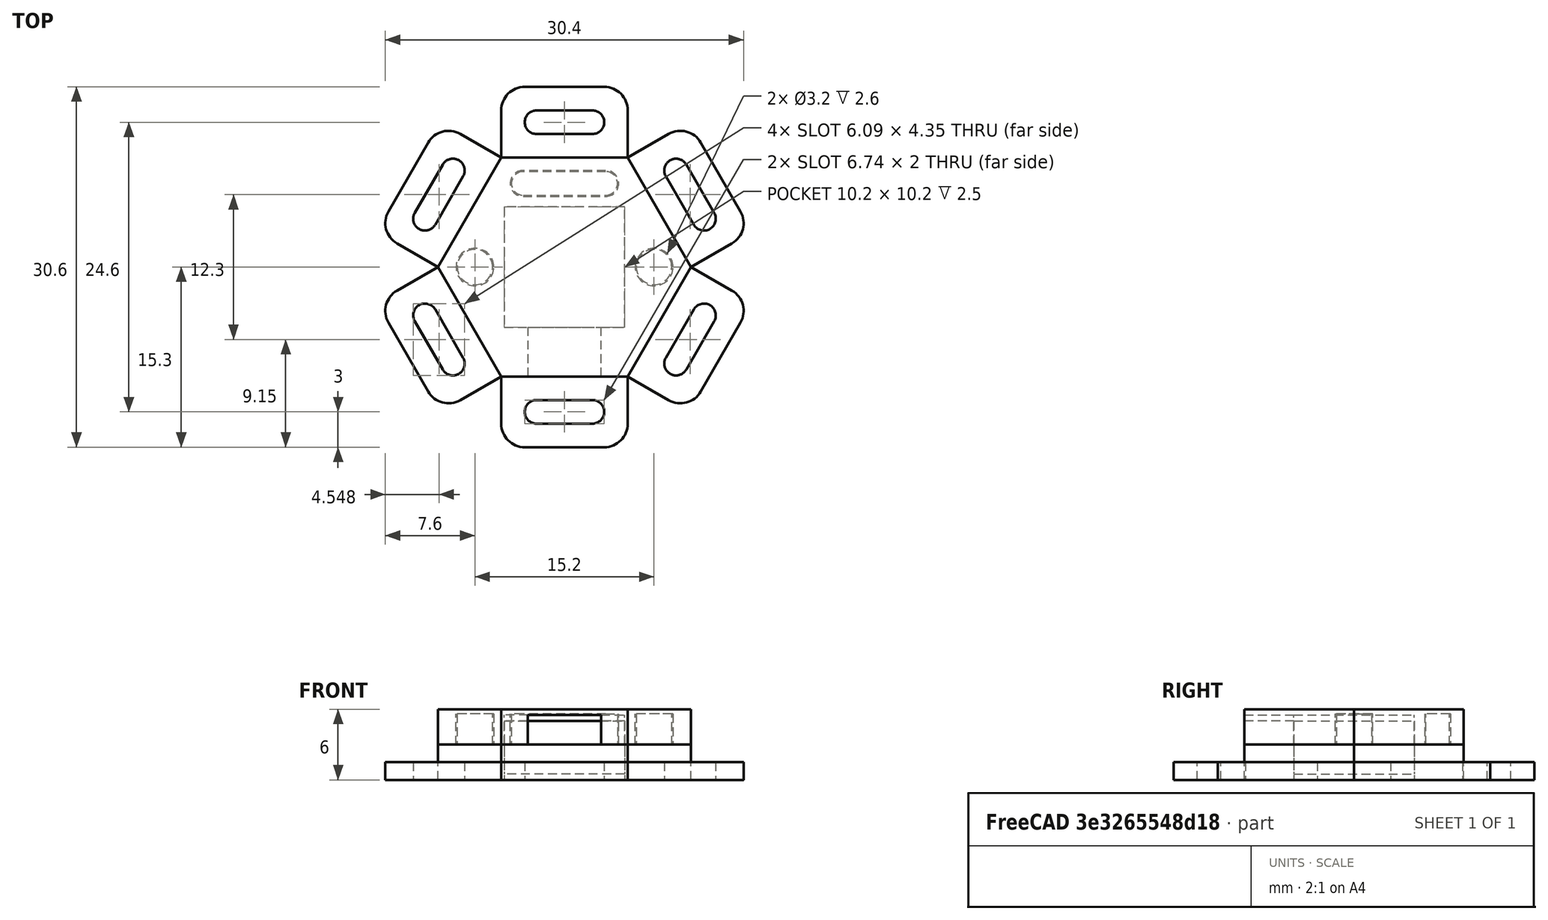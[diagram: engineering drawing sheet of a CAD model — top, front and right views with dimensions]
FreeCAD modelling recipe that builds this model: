
FCSTD DOCUMENT  (FreeCAD 1.0R39109 (Git))
Label: vybronics_hexagon
License: Creative Commons Attribution 4.0
LicenseURL: https://creativecommons.org/licenses/by/4.0/
objects: TechDraw::DrawViewDimension×15, TechDraw::DrawProjGroupItem×8, Sketcher::SketchObject×7, PartDesign::SubShapeBinder×7, PartDesign::Body×6, PartDesign::Pad×5, PartDesign::Pocket×3, PartDesign::FeatureBase×2, PartDesign::Plane×2, TechDraw::DrawProjGroup×2, PartDesign::Boolean×1, Part::FeaturePython×1, Part::Compound×1, TechDraw::DrawSVGTemplate×1, TechDraw::DrawViewImage×1, TechDraw::DrawPage×1
note: 82 computed .brp shape members not serialized (recipe doc carries the construction recipe); baked Part::Feature solids carry a one-line shape summary decoded from their .brp

FEATURE [Sketcher::SketchObject] Sketch
  ArcFitTolerance = 0
  AttachmentSupport = -> [XY_Plane]
  FullyConstrained = true
  MakeInternals = false
  MapMode = 5
  sketch-geometry (5):
    g0: LineSegment StartX=5.1 StartY=-5.1 StartZ=0 EndX=5.1 EndY=5.1 EndZ=0
    g1: LineSegment StartX=5.1 StartY=5.1 StartZ=0 EndX=-5.1 EndY=5.1 EndZ=0
    g2: LineSegment StartX=-5.1 StartY=5.1 StartZ=0 EndX=-5.1 EndY=-5.1 EndZ=0
    g3: LineSegment StartX=-5.1 StartY=-5.1 StartZ=0 EndX=5.1 EndY=-5.1 EndZ=0
    g4: GeomPoint [constr] X=0 Y=-1e-16 Z=0
  constraints (12):
    c: Coincident(g0,g1)
    c: Coincident(g1,g2)
    c: Coincident(g2,g3)
    c: Coincident(g3,g0)
    c: Horizontal(g1)
    c: Horizontal(g3)
    c: Vertical(g0)
    c: Vertical(g2)
    c: Symmetric(g1,g0,g4)
    c: Coincident(g4,g-1)
    c: DistanceX(g1,g1) = 10.2
    c: DistanceY(g0,g0) = 10.2
FEATURE [PartDesign::Pad] Pad
  Direction = (0,0,1)
  Length = 5
  Length2 = 10
  Profile = -> Sketch
  ReferenceAxis = -> Sketch [N_Axis]
  Suppressed = false
  Type = 0
FEATURE [PartDesign::Body] Body
  AllowCompound = false
  Group = -> [Sketch,Pad]
  Origin = -> Origin
  Tip = -> Pad
FEATURE [PartDesign::SubShapeBinder] Binder  label="actuator_area"
  BindCopyOnChange = 0
  BindMode = 0
  ClaimChildren = false
  Context = -> Body001 [Binder.]
  Fuse = false
  MakeFace = true
  OffsetFill = false
  OffsetIntersection = false
  OffsetJoinType = 0
  OffsetOpenResult = false
  PartialLoad = false
  Relative = true
  Support = -> [Body[Pad.Face5]]
  _Version = 2
FEATURE [Sketcher::SketchObject] Sketch001
  ArcFitTolerance = 0
  AttachmentSupport = -> [XY_Plane001]
  ExternalGeometry = -> [Binder]
  FullyConstrained = true
  MakeInternals = false
  MapMode = 5
  sketch-geometry (5):
    g0: LineSegment StartX=-3.1 StartY=-5.1 StartZ=0 EndX=-3.1 EndY=-9.3 EndZ=0
    g1: LineSegment StartX=-3.1 StartY=-9.3 StartZ=0 EndX=3.1 EndY=-9.3 EndZ=0
    g2: LineSegment StartX=3.1 StartY=-9.3 StartZ=0 EndX=3.1 EndY=-5.1 EndZ=0
    g3: LineSegment StartX=3.1 StartY=-5.1 StartZ=0 EndX=-3.1 EndY=-5.1 EndZ=0
    g4: GeomPoint [constr] X=0 Y=-7.2 Z=0
  constraints (13):
    c: Coincident(g0,g1)
    c: Coincident(g1,g2)
    c: Coincident(g2,g3)
    c: Coincident(g3,g0)
    c: Horizontal(g1)
    c: Horizontal(g3)
    c: Vertical(g0)
    c: Vertical(g2)
    c: Symmetric(g1,g0,g4)
    c: PointOnObject(g4,g-2)
    c: PointOnObject(g0,g-4)
    c: DistanceX(g1,g1) = 6.2
    c: DistanceY(g2,g2) = 4.2
FEATURE [PartDesign::Pad] Pad001
  Direction = (0,0,1)
  Length = 2
  Length2 = 10
  Profile = -> Sketch001
  ReferenceAxis = -> Sketch001 [N_Axis]
  Suppressed = false
  Type = 0
FEATURE [PartDesign::Boolean] Boolean
  BaseFeature = -> Pad001
  Group = -> [Body]
  Suppressed = false
  Type = 0
  UsePlacement = false
FEATURE [PartDesign::Body] Body001  label="actuator"
  AllowCompound = false
  Group = -> [Sketch001,Binder,Pad001,Boolean]
  Origin = -> Origin001
  Placement = pos=(-6e-16,0,5) rot=(0,1,0;3.14159rad)
  Tip = -> Boolean
FEATURE [PartDesign::SubShapeBinder] Binder001
  BindCopyOnChange = 0
  BindMode = 0
  ClaimChildren = false
  Context = -> Body002 [Binder001.]
  Fuse = false
  MakeFace = true
  OffsetFill = false
  OffsetIntersection = false
  OffsetJoinType = 0
  OffsetOpenResult = false
  PartialLoad = false
  Relative = true
  Support = -> [Body001[Boolean.Face4],Binder002]
  _Version = 2
FEATURE [Sketcher::SketchObject] Sketch002
  ArcFitTolerance = 0
  AttachmentSupport = -> [XY_Plane002]
  ExternalGeometry = -> [Binder001]
  FullyConstrained = true
  MakeInternals = false
  MapMode = 5
  sketch-geometry (14):
    g0: LineSegment [constr] StartX=-5.1 StartY=5.1 StartZ=0 EndX=5.1 EndY=5.1 EndZ=0
    g1: LineSegment [constr] StartX=5.1 StartY=5.1 StartZ=0 EndX=5.1 EndY=-9.3 EndZ=0
    g2: LineSegment [constr] StartX=5.1 StartY=-9.3 StartZ=0 EndX=-5.1 EndY=-9.3 EndZ=0
    g3: LineSegment [constr] StartX=-5.1 StartY=-9.3 StartZ=0 EndX=-5.1 EndY=5.1 EndZ=0
    g4: LineSegment [constr] StartX=5.1 StartY=5.1 StartZ=0 EndX=-5.1 EndY=-9.3 EndZ=0
    g5: LineSegment [constr] StartX=-5.1 StartY=5.1 StartZ=0 EndX=5.1 EndY=-9.3 EndZ=0
    g6: GeomPoint [constr] X=0 Y=-2.1 Z=0
    g7: LineSegment StartX=-5.36936 StartY=9.3 StartZ=0 EndX=-10.7387 EndY=1.2e-15 EndZ=0
    g8: LineSegment StartX=-10.7387 StartY=1.2e-15 StartZ=0 EndX=-5.36936 EndY=-9.3 EndZ=0
    g9: LineSegment StartX=-5.36936 StartY=-9.3 StartZ=0 EndX=5.36936 EndY=-9.3 EndZ=0
    g10: LineSegment StartX=5.36936 StartY=-9.3 StartZ=0 EndX=10.7387 EndY=1.9e-15 EndZ=0
    g11: LineSegment StartX=10.7387 StartY=1.9e-15 StartZ=0 EndX=5.36936 EndY=9.3 EndZ=0
    g12: LineSegment StartX=5.36936 StartY=9.3 StartZ=0 EndX=-5.36936 EndY=9.3 EndZ=0
    g13: Circle [constr] CenterX=0 CenterY=0 CenterZ=0 NormalX=0 NormalY=0 NormalZ=1 AngleXU=0 Radius=10.7387
  constraints (31):
    c: Coincident(g0,g1)
    c: Coincident(g1,g2)
    c: Coincident(g2,g3)
    c: Coincident(g3,g0)
    c: Horizontal(g2)
    c: Vertical(g1)
    c: Vertical(g3)
    c: Coincident(g0,g-5)
    c: Coincident(g0,g-4)
    c: PointOnObject(g1,g-9)
    c: Coincident(g4,g0)
    c: Coincident(g4,g2)
    c: Coincident(g5,g0)
    c: Coincident(g5,g1)
    c: PointOnObject(g6,g5)
    c: PointOnObject(g6,g-2)
    c: Coincident(g7,g8)
    c: Coincident(g8,g9)
    c: Coincident(g9,g10)
    c: Coincident(g10,g11)
    c: Coincident(g11,g12)
    c: Coincident(g12,g7)
    c: Equal(g7, g8-g12) x5
    c: PointOnObject(g7,g13)
    c: PointOnObject(g8,g13)
    c: PointOnObject(g9,g13)
    c: PointOnObject(g10,g13)
    c: PointOnObject(g11,g13)
    c: PointOnObject(g12,g13)
    c: Coincident(g13,g-1)
    c: Tangent(g9,g2)
FEATURE [PartDesign::SubShapeBinder] Binder002
  BindCopyOnChange = 0
  BindMode = 0
  ClaimChildren = false
  Context = -> Body002 [Binder002.]
  Fuse = false
  MakeFace = true
  OffsetFill = false
  OffsetIntersection = false
  OffsetJoinType = 0
  OffsetOpenResult = false
  PartialLoad = false
  Relative = true
  Support = -> [Body001[Boolean.Face10]]
  _Version = 2
FEATURE [PartDesign::Pad] Pad002
  Direction = (0,0,1)
  Length = 3
  Length2 = 10
  Profile = -> Sketch002
  ReferenceAxis = -> Sketch002 [N_Axis]
  Suppressed = false
  Type = 0
FEATURE [PartDesign::Body] Body002
  AllowCompound = false
  Group = -> [Binder001,Sketch002,Binder002,Pad002]
  Origin = -> Origin002
  Placement = pos=(0,0,3) rot=(0,0,1;0rad)
  Tip = -> Pad002
FEATURE [PartDesign::FeatureBase] Clone
  BaseFeature = -> Body002
  Suppressed = false
FEATURE [PartDesign::SubShapeBinder] Binder003
  BindCopyOnChange = 0
  BindMode = 0
  ClaimChildren = false
  Context = -> Body004 [Binder003.]
  Fuse = false
  MakeFace = true
  OffsetFill = false
  OffsetIntersection = false
  OffsetJoinType = 0
  OffsetOpenResult = false
  PartialLoad = false
  Relative = true
  Support = -> [Body003[Clone.Face7]]
  _Version = 2
FEATURE [Sketcher::SketchObject] Sketch003
  ArcFitTolerance = 0
  AttachmentSupport = -> [XY_Plane004]
  ExternalGeometry = -> [Binder003]
  FullyConstrained = true
  MakeInternals = false
  MapMode = 5
  sketch-geometry (10):
    g0: LineSegment StartX=-5.36936 StartY=9.3 StartZ=0 EndX=5.36936 EndY=9.3 EndZ=0
    g1: LineSegment StartX=5.36936 StartY=9.3 StartZ=0 EndX=5.36936 EndY=13.3 EndZ=0
    g2: LineSegment StartX=3.36936 StartY=15.3 StartZ=0 EndX=-3.36936 EndY=15.3 EndZ=0
    g3: LineSegment StartX=-5.36936 StartY=13.3 StartZ=0 EndX=-5.36936 EndY=9.3 EndZ=0
    g4: ArcOfCircle CenterX=-3.36936 CenterY=13.3 CenterZ=0 NormalX=0 NormalY=0 NormalZ=1 AngleXU=0 Radius=2 StartAngle=1.5708 EndAngle=3.14159
    g5: ArcOfCircle CenterX=3.36936 CenterY=13.3 CenterZ=0 NormalX=0 NormalY=0 NormalZ=1 AngleXU=0 Radius=2 StartAngle=2e-16 EndAngle=1.5708
    g6: ArcOfCircle CenterX=-2.36936 CenterY=12.3 CenterZ=0 NormalX=0 NormalY=0 NormalZ=1 AngleXU=0 Radius=1 StartAngle=1.5708 EndAngle=4.71239
    g7: ArcOfCircle CenterX=2.36936 CenterY=12.3 CenterZ=0 NormalX=0 NormalY=0 NormalZ=1 AngleXU=0 Radius=1 StartAngle=4.71239 EndAngle=7.85398
    g8: LineSegment StartX=-2.36936 StartY=11.3 StartZ=0 EndX=2.36936 EndY=11.3 EndZ=0
    g9: LineSegment StartX=2.36936 StartY=13.3 StartZ=0 EndX=-2.36936 EndY=13.3 EndZ=0
  constraints (23):
    c: Coincident(g0,g1)
    c: Coincident(g3,g0)
    c: Horizontal(g2)
    c: Vertical(g1)
    c: Vertical(g3)
    c: Coincident(g0,g-3)
    c: Coincident(g0,g-3)
    c: Tangent(g2,g4) = -1.5708
    c: Tangent(g3,g4) = -1.5708
    c: Tangent(g1,g5) = -1.5708
    c: Tangent(g2,g5) = -1.5708
    c: Radius(g4) = 2
    c: Equal(g5,g4)
    c: DistanceY(g1,g1) = 4
    c: Tangent(g6,g8) = -1.5708
    c: Tangent(g8,g7) = -1.5708
    c: Tangent(g7,g9) = -1.5708
    c: Tangent(g9,g6) = -1.5708
    c: Equal(g6,g7)
    c: Symmetric(g6,g7,g-2)
    c: DistanceY(g6,g2) = 2
    c: Radius(g7) = 1
    c: DistanceX(g7,g0) = 3
FEATURE [PartDesign::Pad] Pad003
  Direction = (0,0,1)
  Length = 1.5
  Length2 = 10
  Profile = -> Sketch003
  ReferenceAxis = -> Sketch003 [N_Axis]
  Suppressed = false
  Type = 0
FEATURE [PartDesign::Body] Body004
  AllowCompound = false
  Group = -> [Binder003,Sketch003,Pad003]
  Origin = -> Origin004
  Tip = -> Pad003
FEATURE [Part::FeaturePython] Array  label="bottom_holder"  # Draft array (typed FeaturePython)
  AlwaysSyncPlacement = false
  Angle = 360
  ArrayType = 1
  Axis = (0,0,1)
  Base = -> Body004
  Center = (0,0,0)
  Count = 6
  ExpandArray = false
  Fuse = true
  IntervalAxis = (0,0,0)
  IntervalX = (50,0,0)
  IntervalY = (0,50,0)
  IntervalZ = (0,0,50)
  NumberCircles = 3
  NumberPolar = 6
  NumberX = 2
  NumberY = 2
  NumberZ = 1
  PlacementList = 6 placements: [(0,0,0),(0,0,0),(0,0,0),(0,0,0),(0,0,0),(0,0,0)]
  RadialDistance = 50
  ScaleList = (6) [(1,1,1),(1,1,1),(1,1,1),(1,1,1),(1,1,1),(1,1,1)]
  Symmetry = 1
  TangentialDistance = 25
FEATURE [PartDesign::Plane] DatumPlane
  AttachmentSupport = -> [Clone]
  Length = 60
  MapMode = 5
  Placement = pos=(0,0,3) rot=(0,0,1;0rad)
  ResizeMode = 0
  Width = 60
FEATURE [PartDesign::SubShapeBinder] Binder004
  BindCopyOnChange = 0
  BindMode = 0
  ClaimChildren = false
  Context = -> Body003 [Binder004.]
  Fuse = false
  MakeFace = true
  OffsetFill = false
  OffsetIntersection = false
  OffsetJoinType = 0
  OffsetOpenResult = false
  PartialLoad = false
  Relative = true
  Support = -> [Body001[Boolean.Face4]]
  _Version = 2
FEATURE [Sketcher::SketchObject] Sketch004
  ArcFitTolerance = 0
  AttachmentSupport = -> [DatumPlane]
  ExternalGeometry = -> [Binder004]
  FullyConstrained = true
  MakeInternals = false
  MapMode = 5
  Placement = pos=(0,0,3) rot=(0,0,1;0rad)
  sketch-geometry (6):
    g0: Circle CenterX=-7.6 CenterY=0 CenterZ=0 NormalX=0 NormalY=0 NormalZ=1 AngleXU=0 Radius=1.5
    g1: Circle CenterX=7.6 CenterY=0 CenterZ=0 NormalX=0 NormalY=0 NormalZ=1 AngleXU=0 Radius=1.5
    g2: ArcOfCircle CenterX=-3.5 CenterY=7.1 CenterZ=0 NormalX=0 NormalY=0 NormalZ=1 AngleXU=0 Radius=1 StartAngle=1.5708 EndAngle=4.71239
    g3: ArcOfCircle CenterX=3.5 CenterY=7.1 CenterZ=0 NormalX=0 NormalY=0 NormalZ=1 AngleXU=0 Radius=1 StartAngle=4.71239 EndAngle=7.85398
    g4: LineSegment StartX=-3.5 StartY=6.1 StartZ=0 EndX=3.5 EndY=6.1 EndZ=0
    g5: LineSegment StartX=3.5 StartY=8.1 StartZ=0 EndX=-3.5 EndY=8.1 EndZ=0
  constraints (15):
    c: PointOnObject(g0,g-1)
    c: Diameter(g0) = 3
    c: Equal(g0,g1) = 3
    c: Distance(g0,g-4) = 1
    c: PointOnObject(g1,g-1)
    c: Distance(g1,g-5) = 1
    c: Tangent(g2,g4) = -1.5708
    c: Tangent(g4,g3) = -1.5708
    c: Tangent(g3,g5) = -1.5708
    c: Tangent(g5,g2) = -1.5708
    c: Equal(g2,g3)
    c: Symmetric(g2,g3,g-2)
    c: Radius(g2) = 1
    c: Distance(g2,g-3) = 1
    c: DistanceX(g5,g5) = 7
FEATURE [PartDesign::Pad] Pad004
  BaseFeature = -> Clone
  Direction = (0,0,1)
  Length = 2.6
  Length2 = 10
  Profile = -> Sketch004
  ReferenceAxis = -> Sketch004 [N_Axis]
  Suppressed = false
  Type = 0
FEATURE [PartDesign::FeatureBase] Clone001
  BaseFeature = -> Body002
  Placement = pos=(0,0,3) rot=(0,0,1;0rad)
  Suppressed = false
FEATURE [PartDesign::SubShapeBinder] Binder005
  BindCopyOnChange = 0
  BindMode = 0
  ClaimChildren = false
  Context = -> Body005 [Binder005.]
  Fuse = false
  MakeFace = true
  Offset = 0.1
  OffsetFill = false
  OffsetIntersection = false
  OffsetJoinType = 0
  OffsetOpenResult = false
  PartialLoad = false
  Relative = true
  Support = -> [Body003[Pad004.Face15,Pad004.Face16,Pad004.Face17]]
  _Version = 2
FEATURE [PartDesign::Pocket] Pocket
  BaseFeature = -> Clone001
  Direction = (0,0,-1)
  Length = 5
  Length2 = 5
  Placement = pos=(0,0,3) rot=(0,0,1;0rad)
  Profile = -> Binder005
  Suppressed = false
  Type = 0
FEATURE [Sketcher::SketchObject] Sketch005
  ArcFitTolerance = 0
  AttachmentSupport = -> [DatumPlane]
  ExternalGeometry = -> [Binder004]
  FullyConstrained = true
  MakeInternals = false
  MapMode = 5
  Placement = pos=(0,0,3) rot=(0,0,1;0rad)
  sketch-geometry (5):
    g0: LineSegment StartX=5.1 StartY=-5.1 StartZ=0 EndX=5.1 EndY=5.1 EndZ=0
    g1: LineSegment StartX=5.1 StartY=5.1 StartZ=0 EndX=-5.1 EndY=5.1 EndZ=0
    g2: LineSegment StartX=-5.1 StartY=5.1 StartZ=0 EndX=-5.1 EndY=-5.1 EndZ=0
    g3: LineSegment StartX=-5.1 StartY=-5.1 StartZ=0 EndX=5.1 EndY=-5.1 EndZ=0
    g4: GeomPoint [constr] X=0 Y=0 Z=0
  constraints (11):
    c: Coincident(g0,g1)
    c: Coincident(g1,g2)
    c: Coincident(g2,g3)
    c: Coincident(g3,g0)
    c: Horizontal(g1)
    c: Horizontal(g3)
    c: Vertical(g0)
    c: Vertical(g2)
    c: Symmetric(g1,g0,g4)
    c: Coincident(g4,g-1)
    c: Coincident(g1,g-3)
FEATURE [PartDesign::Pocket] Pocket001
  BaseFeature = -> Pad004
  Direction = (0,0,-1)
  Length = 2.5
  Length2 = 5
  Profile = -> Sketch005
  ReferenceAxis = -> Sketch005 [N_Axis]
  Suppressed = false
  Type = 0
FEATURE [PartDesign::Body] Body003  label="bottom_platform"
  AllowCompound = false
  Group = -> [Clone,DatumPlane,Sketch004,Binder004,Pad004,Sketch005,Pocket001]
  Origin = -> Origin003
  Tip = -> Pocket001
FEATURE [Part::Compound] Compound  label="bottom"
  Links = -> [Body003,Array]
FEATURE [PartDesign::SubShapeBinder] Binder006
  BindCopyOnChange = 0
  BindMode = 0
  ClaimChildren = false
  Context = -> Body005 [Binder006.]
  Fuse = false
  MakeFace = true
  OffsetFill = false
  OffsetIntersection = false
  OffsetJoinType = 0
  OffsetOpenResult = false
  PartialLoad = false
  Relative = true
  Support = -> [Body001[Boolean.Face10,Boolean.Face4]]
  _Version = 2
FEATURE [PartDesign::Plane] DatumPlane001
  AttachmentSupport = -> [Pocket]
  Length = 60
  MapMode = 5
  Placement = pos=(0,0,3) rot=(1,0,0;3.14159rad)
  ResizeMode = 0
  Width = 60
FEATURE [Sketcher::SketchObject] Sketch006
  ArcFitTolerance = 0
  AttachmentSupport = -> [DatumPlane001]
  ExternalGeometry = -> [Binder006]
  FullyConstrained = true
  MakeInternals = false
  MapMode = 5
  Placement = pos=(0,0,3) rot=(1,0,0;3.14159rad)
  sketch-geometry (8):
    g0: LineSegment StartX=-3.1 StartY=9.3 StartZ=0 EndX=3.1 EndY=9.3 EndZ=0
    g1: LineSegment StartX=3.1 StartY=9.3 StartZ=0 EndX=3.1 EndY=5.1 EndZ=0
    g2: LineSegment StartX=3.1 StartY=5.1 StartZ=0 EndX=5.1 EndY=5.1 EndZ=0
    g3: LineSegment StartX=5.1 StartY=5.1 StartZ=0 EndX=5.1 EndY=-5.1 EndZ=0
    g4: LineSegment StartX=5.1 StartY=-5.1 StartZ=0 EndX=-5.1 EndY=-5.1 EndZ=0
    g5: LineSegment StartX=-5.1 StartY=-5.1 StartZ=0 EndX=-5.1 EndY=5.1 EndZ=0
    g6: LineSegment StartX=-5.1 StartY=5.1 StartZ=0 EndX=-3.1 EndY=5.1 EndZ=0
    g7: LineSegment StartX=-3.1 StartY=5.1 StartZ=0 EndX=-3.1 EndY=9.3 EndZ=0
  constraints (16):
    c: Coincident(g-6,g0)
    c: Coincident(g0,g-10)
    c: Coincident(g0,g1)
    c: Coincident(g1,g-10)
    c: Coincident(g1,g2)
    c: Coincident(g2,g-9)
    c: Coincident(g2,g3)
    c: Coincident(g3,g-8)
    c: Coincident(g3,g4)
    c: Coincident(g4,g-7)
    c: Coincident(g4,g5)
    c: Coincident(g5,g-4)
    c: Coincident(g5,g6)
    c: Coincident(g6,g-6)
    c: Coincident(g6,g7)
    c: Coincident(g7,g0)
FEATURE [PartDesign::Pocket] Pocket002
  BaseFeature = -> Pocket
  Direction = (0,0,1)
  Length = 2.5
  Length2 = 5
  Placement = pos=(0,0,3) rot=(0,0,1;0rad)
  Profile = -> Sketch006
  ReferenceAxis = -> Sketch006 [N_Axis]
  Suppressed = false
  Type = 0
FEATURE [PartDesign::Body] Body005  label="top"
  AllowCompound = false
  Group = -> [Clone001,Binder005,Pocket,Binder006,DatumPlane001,Sketch006,Pocket002]
  Origin = -> Origin005
  Tip = -> Pocket002
FEATURE [TechDraw::DrawSVGTemplate] Template
  EditableTexts = Designed_by_Name=Dennis Wittchen; Drawing_number=1; FC-Date=Jan 17 2024; FC-SC=Scale; FC-SH=1; FC-Title=Vybronics case; Subtitle=modular system; Weight=Weight
  Height = 210
  Orientation = 1
  Template = /Applications/FreeCAD.app/Contents/Resources/share/Mod/TechDraw/Templates/A4_LandscapeTD.svg
  Width = 297
FEATURE [TechDraw::DrawViewImage] ActiveView
  Height = 100
  ImageFile = <userpath>/Library/Caches/FreeCAD/Cache/FreeCAD_Doc_c7f0712c-06d2-497b-9420-8f54370957ff_efbe33_32540/PageActiveView41v21o.png
  LockPosition = false
  Rotation = 0
  Scale = 2
  ScaleType = 2
  Width = 100
  X = 245.698
  Y = 86.6817
FEATURE [TechDraw::DrawProjGroupItem] ProjItem  label="Front"
  CoarseView = false
  Direction = (0,0,1)
  Focus = 100
  HardHidden = false
  IsoCount = 0
  IsoHidden = false
  IsoVisible = false
  LockPosition = true
  Perspective = false
  Rotation = 0
  RotationVector = (1,0,0)
  Scale = 2
  ScaleType = 2
  ScrubCount = 0
  SeamHidden = false
  SeamVisible = false
  SmoothHidden = false
  SmoothVisible = true
  Source = -> [Body005]
  Type = 0
  X = 0
  XDirection = (1,0,0)
  Y = 0
FEATURE [TechDraw::DrawProjGroupItem] ProjItem001  label="Bottom"
  CoarseView = false
  Direction = (0,-1,0)
  Focus = 100
  HardHidden = false
  IsoCount = 0
  IsoHidden = false
  IsoVisible = false
  LockPosition = false
  Perspective = false
  Rotation = 0
  RotationVector = (1,0,0)
  Scale = 2
  ScaleType = 2
  ScrubCount = 0
  SeamHidden = false
  SeamVisible = false
  SmoothHidden = false
  SmoothVisible = true
  Source = -> [Body005]
  Type = 5
  X = 0
  XDirection = (1,0,0)
  Y = 33.9717
FEATURE [TechDraw::DrawProjGroupItem] ProjItem002  label="Rear"
  CoarseView = false
  Direction = (0,0,-1)
  Focus = 100
  HardHidden = false
  IsoCount = 0
  IsoHidden = false
  IsoVisible = false
  LockPosition = false
  Perspective = false
  Rotation = 0
  RotationVector = (1,0,0)
  Scale = 2
  ScaleType = 2
  ScrubCount = 0
  SeamHidden = false
  SeamVisible = false
  SmoothHidden = false
  SmoothVisible = true
  Source = -> [Body005]
  Type = 3
  X = 46.4774
  XDirection = (-1,0,0)
  Y = 0
FEATURE [TechDraw::DrawProjGroup] ProjGroup
  Anchor = -> ProjItem
  AutoDistribute = false
  LockPosition = false
  ProjectionType = 0
  Rotation = 0
  Scale = 2
  ScaleType = 2
  Source = -> [Body005]
  Views = -> [ProjItem,ProjItem001,ProjItem002]
  X = 42.3498
  Y = 45.659
  spacingX = 25
  spacingY = 25
FEATURE [TechDraw::DrawViewDimension] Dimension
  AngleOverride = false
  Arbitrary = false
  ArbitraryTolerances = false
  EqualTolerance = true
  ExtensionAngle = 0
  FormatSpec = %.2w
  FormatSpecOverTolerance = %+.2w
  FormatSpecUnderTolerance = %+.2w
  Inverted = false
  LineAngle = 0
  LockPosition = false
  MeasureType = 1
  OverTolerance = 0
  References2D = -> [ProjItem]
  Rotation = 0
  ScaleType = 0
  TheoreticalExact = false
  Type = 0
  UnderTolerance = 0
  X = -22.3709
  Y = 14.2955
FEATURE [TechDraw::DrawViewDimension] Dimension001
  AngleOverride = false
  Arbitrary = false
  ArbitraryTolerances = false
  EqualTolerance = true
  ExtensionAngle = 0
  FormatSpec = %.2w
  FormatSpecOverTolerance = %+.2w
  FormatSpecUnderTolerance = %+.2w
  Inverted = false
  LineAngle = 0
  LockPosition = false
  MeasureType = 1
  OverTolerance = 0
  References2D = -> [ProjItem]
  Rotation = 0
  ScaleType = 0
  TheoreticalExact = false
  Type = 1
  UnderTolerance = 0
  X = -1.45647
  Y = -26.1729
FEATURE [TechDraw::DrawViewDimension] Dimension003
  AngleOverride = false
  Arbitrary = false
  ArbitraryTolerances = false
  EqualTolerance = true
  ExtensionAngle = 0
  FormatSpec = %.2w
  FormatSpecOverTolerance = %+.2w
  FormatSpecUnderTolerance = %+.2w
  Inverted = false
  LineAngle = 0
  LockPosition = false
  MeasureType = 1
  OverTolerance = 0
  References2D = -> [ProjItem002]
  Rotation = 0
  ScaleType = 0
  TheoreticalExact = false
  Type = 2
  UnderTolerance = 0
  X = 20.0557
  Y = -12.9
FEATURE [TechDraw::DrawViewDimension] Dimension004
  AngleOverride = false
  Arbitrary = false
  ArbitraryTolerances = false
  EqualTolerance = true
  ExtensionAngle = 0
  FormatSpec = %.2w
  FormatSpecOverTolerance = %+.2w
  FormatSpecUnderTolerance = %+.2w
  Inverted = false
  LineAngle = 0
  LockPosition = false
  MeasureType = 1
  OverTolerance = 0
  References2D = -> [ProjItem002]
  Rotation = 0
  ScaleType = 0
  TheoreticalExact = false
  Type = 2
  UnderTolerance = 0
  X = 28.0315
  Y = -7.11407
FEATURE [TechDraw::DrawViewDimension] Dimension005
  AngleOverride = false
  Arbitrary = false
  ArbitraryTolerances = false
  EqualTolerance = true
  ExtensionAngle = 0
  FormatSpec = %.2w
  FormatSpecOverTolerance = %+.2w
  FormatSpecUnderTolerance = %+.2w
  Inverted = false
  LineAngle = 0
  LockPosition = false
  MeasureType = 1
  OverTolerance = 0
  References2D = -> [ProjItem002]
  Rotation = 0
  ScaleType = 0
  TheoreticalExact = false
  Type = 2
  UnderTolerance = 0
  X = 35.3626
  Y = -1.87689
FEATURE [TechDraw::DrawViewDimension] Dimension006
  AngleOverride = false
  Arbitrary = false
  ArbitraryTolerances = false
  EqualTolerance = true
  ExtensionAngle = 0
  FormatSpec = %.2w
  FormatSpecOverTolerance = %+.2w
  FormatSpecUnderTolerance = %+.2w
  Inverted = false
  LineAngle = 0
  LockPosition = false
  MeasureType = 1
  OverTolerance = 0
  References2D = -> [ProjItem002]
  Rotation = 0
  ScaleType = 0
  TheoreticalExact = false
  Type = 2
  UnderTolerance = 0
  X = 41.5821
  Y = -1.38844
FEATURE [TechDraw::DrawViewDimension] Dimension007
  AngleOverride = false
  Arbitrary = false
  ArbitraryTolerances = false
  EqualTolerance = true
  ExtensionAngle = 0
  FormatSpec = %.2w
  FormatSpecOverTolerance = %+.2w
  FormatSpecUnderTolerance = %+.2w
  Inverted = false
  LineAngle = 0
  LockPosition = false
  MeasureType = 1
  OverTolerance = 0
  References2D = -> [ProjItem002]
  Rotation = 0
  ScaleType = 0
  TheoreticalExact = false
  Type = 2
  UnderTolerance = 0
  X = 48.3042
  Y = -1.24622
FEATURE [TechDraw::DrawViewDimension] Dimension008
  AngleOverride = false
  Arbitrary = false
  ArbitraryTolerances = false
  EqualTolerance = true
  ExtensionAngle = 0
  FormatSpec = %.2w
  FormatSpecOverTolerance = %+.2w
  FormatSpecUnderTolerance = %+.2w
  Inverted = false
  LineAngle = 0
  LockPosition = false
  MeasureType = 1
  OverTolerance = 0
  References2D = -> [ProjItem002]
  Rotation = 0
  ScaleType = 0
  TheoreticalExact = false
  Type = 1
  UnderTolerance = 0
  X = -0.10144
  Y = 32.2498
FEATURE [TechDraw::DrawViewDimension] Dimension009
  AngleOverride = false
  Arbitrary = false
  ArbitraryTolerances = false
  EqualTolerance = true
  ExtensionAngle = 0
  FormatSpec = %.2w
  FormatSpecOverTolerance = %+.2w
  FormatSpecUnderTolerance = %+.2w
  Inverted = false
  LineAngle = 0
  LockPosition = false
  MeasureType = 1
  OverTolerance = 0
  References2D = -> [ProjItem002]
  Rotation = 0
  ScaleType = 0
  TheoreticalExact = false
  Type = 1
  UnderTolerance = 0
  X = 0.065696
  Y = 38.0801
FEATURE [TechDraw::DrawViewDimension] Dimension010
  AngleOverride = false
  Arbitrary = false
  ArbitraryTolerances = false
  EqualTolerance = true
  ExtensionAngle = 0
  FormatSpec = R%.2w
  FormatSpecOverTolerance = %+.2w
  FormatSpecUnderTolerance = %+.2w
  Inverted = false
  LineAngle = 0
  LockPosition = false
  MeasureType = 1
  OverTolerance = 0
  References2D = -> [ProjItem002]
  Rotation = 0
  ScaleType = 0
  TheoreticalExact = false
  Type = 4
  UnderTolerance = 0
  X = 21.9496
  Y = 26.0651
FEATURE [TechDraw::DrawViewDimension] Dimension011
  AngleOverride = false
  Arbitrary = false
  ArbitraryTolerances = false
  EqualTolerance = true
  ExtensionAngle = 0
  FormatSpec = ⌀%.2w
  FormatSpecOverTolerance = %+.2w
  FormatSpecUnderTolerance = %+.2w
  Inverted = false
  LineAngle = 0
  LockPosition = false
  MeasureType = 1
  OverTolerance = 0
  References2D = -> [ProjItem002]
  Rotation = 0
  ScaleType = 0
  TheoreticalExact = false
  Type = 5
  UnderTolerance = 0
  X = -18.3828
  Y = 16.8737
FEATURE [TechDraw::DrawViewDimension] Dimension012
  AngleOverride = false
  Arbitrary = false
  ArbitraryTolerances = false
  EqualTolerance = true
  ExtensionAngle = 0
  FormatSpec = %.2w
  FormatSpecOverTolerance = %+.2w
  FormatSpecUnderTolerance = %+.2w
  Inverted = false
  LineAngle = 0
  LockPosition = false
  MeasureType = 1
  OverTolerance = 0
  References2D = -> [ProjItem001]
  Rotation = 0
  ScaleType = 0
  TheoreticalExact = false
  Type = 2
  UnderTolerance = 0
  X = -30.111
  Y = -4.45421
FEATURE [TechDraw::DrawViewDimension] Dimension013
  AngleOverride = false
  Arbitrary = false
  ArbitraryTolerances = false
  EqualTolerance = true
  ExtensionAngle = 0
  FormatSpec = %.2w
  FormatSpecOverTolerance = %+.2w
  FormatSpecUnderTolerance = %+.2w
  Inverted = false
  LineAngle = 0
  LockPosition = false
  MeasureType = 1
  OverTolerance = 0
  References2D = -> [ProjItem002]
  Rotation = 0
  ScaleType = 0
  TheoreticalExact = false
  Type = 1
  UnderTolerance = 0
  X = -0.62023
  Y = -28.1773
FEATURE [TechDraw::DrawProjGroupItem] ProjItem003  label="Front001"
  CoarseView = false
  Direction = (0,0,1)
  Focus = 100
  HardHidden = false
  IsoCount = 0
  IsoHidden = false
  IsoVisible = false
  LockPosition = true
  Perspective = false
  Rotation = 0
  RotationVector = (1,0,0)
  Scale = 2
  ScaleType = 2
  ScrubCount = 0
  SeamHidden = false
  SeamVisible = false
  SmoothHidden = false
  SmoothVisible = true
  Source = -> [Compound]
  Type = 0
  X = 0
  XDirection = (1,0,0)
  Y = 0
FEATURE [TechDraw::DrawProjGroupItem] ProjItem004  label="Bottom001"
  CoarseView = false
  Direction = (0,-1,0)
  Focus = 100
  HardHidden = false
  IsoCount = 0
  IsoHidden = false
  IsoVisible = false
  LockPosition = false
  Perspective = false
  Rotation = 0
  RotationVector = (1,0,0)
  Scale = 2
  ScaleType = 2
  ScrubCount = 0
  SeamHidden = false
  SeamVisible = false
  SmoothHidden = false
  SmoothVisible = true
  Source = -> [Compound]
  Type = 5
  X = 0
  XDirection = (1,0,0)
  Y = 47.3852
FEATURE [TechDraw::DrawProjGroupItem] ProjItem005  label="Right"
  CoarseView = false
  Direction = (1,0,1e-16)
  Focus = 100
  HardHidden = false
  IsoCount = 0
  IsoHidden = false
  IsoVisible = false
  LockPosition = false
  Perspective = false
  Rotation = 0
  RotationVector = (1,0,0)
  Scale = 2
  ScaleType = 2
  ScrubCount = 0
  SeamHidden = false
  SeamVisible = false
  SmoothHidden = false
  SmoothVisible = true
  Source = -> [Compound]
  Type = 2
  X = -52.3167
  XDirection = (1e-16,0,-1)
  Y = 0
FEATURE [TechDraw::DrawProjGroupItem] ProjItem007  label="FrontBottomLeft"
  CoarseView = false
  Direction = (-0.57735,-0.57735,0.57735)
  Focus = 100
  HardHidden = false
  IsoCount = 0
  IsoHidden = false
  IsoVisible = false
  LockPosition = false
  Perspective = false
  Rotation = 0
  RotationVector = (1,0,0)
  Scale = 2
  ScaleType = 2
  ScrubCount = 0
  SeamHidden = false
  SeamVisible = false
  SmoothHidden = false
  SmoothVisible = true
  Source = -> [Compound]
  Type = 8
  X = 149.424
  XDirection = (0.707107,0,0.707107)
  Y = 22.1656
FEATURE [TechDraw::DrawProjGroupItem] ProjItem006  label="Rear001"
  CoarseView = false
  Direction = (0,0,-1)
  Focus = 100
  HardHidden = false
  IsoCount = 0
  IsoHidden = false
  IsoVisible = false
  LockPosition = false
  Perspective = false
  Rotation = 0
  RotationVector = (1,0,0)
  Scale = 2
  ScaleType = 2
  ScrubCount = 0
  SeamHidden = false
  SeamVisible = false
  SmoothHidden = false
  SmoothVisible = true
  Source = -> [Compound]
  Type = 3
  X = 73.4035
  XDirection = (-1,0,0)
  Y = 0
FEATURE [TechDraw::DrawProjGroup] ProjGroup001
  Anchor = -> ProjItem003
  AutoDistribute = false
  LockPosition = false
  ProjectionType = 0
  Rotation = 0
  Scale = 2
  ScaleType = 2
  Source = -> [Compound]
  Views = -> [ProjItem003,ProjItem004,ProjItem005,ProjItem006,ProjItem007]
  X = 80.9332
  Y = 135.076
  spacingX = 15
  spacingY = 15
FEATURE [TechDraw::DrawViewDimension] Dimension014
  AngleOverride = false
  Arbitrary = false
  ArbitraryTolerances = false
  EqualTolerance = true
  ExtensionAngle = 0
  FormatSpec = %.2w
  FormatSpecOverTolerance = %+.2w
  FormatSpecUnderTolerance = %+.2w
  Inverted = false
  LineAngle = 0
  LockPosition = false
  MeasureType = 1
  OverTolerance = 0
  References2D = -> [ProjItem006]
  Rotation = 0
  ScaleType = 0
  TheoreticalExact = false
  Type = 1
  UnderTolerance = 0
  X = -0.562374
  Y = -45.0781
FEATURE [TechDraw::DrawViewDimension] Dimension015
  AngleOverride = false
  Arbitrary = false
  ArbitraryTolerances = false
  EqualTolerance = true
  ExtensionAngle = 0
  FormatSpec = %.2w
  FormatSpecOverTolerance = %+.2w
  FormatSpecUnderTolerance = %+.2w
  Inverted = false
  LineAngle = 0
  LockPosition = false
  MeasureType = 1
  OverTolerance = 0
  References2D = -> [ProjItem006]
  Rotation = 0
  ScaleType = 0
  TheoreticalExact = false
  Type = 1
  UnderTolerance = 0
  X = -0.140594
  Y = -37.0504
FEATURE [TechDraw::DrawPage] Page  label="documentation"
  KeepUpdated = true
  NextBalloonIndex = 1
  ProjectionType = 0
  Template = -> Template
  Views = -> [ActiveView,ProjGroup,Dimension,Dimension001,Dimension003,Dimension004,Dimension005,Dimension006,Dimension007,Dimension008,Dimension009,Dimension010,Dimension011,Dimension012,Dimension013,ProjGroup001,Dimension014,Dimension015]
